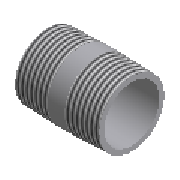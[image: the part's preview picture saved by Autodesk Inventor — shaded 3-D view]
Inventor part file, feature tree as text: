
AUTODESK INVENTOR PART (.ipt)
format: ipt  version: 2023.2 (Build 272271030, 271C)  size: 187,392 bytes
history: native  units: mm (DEFAULTED — no unit token found)
features: other x6, revolve x1, sketch x1
ambient origin geometry x8: Origin, YZ Plane, XZ Plane, XY Plane, X Axis, Y Axis, Z Axis, Center Point
bodies: Solid1 (feature_tree)
feature tree (8):
  revolve  "Revolution1"  [1 undecoded]
  other  "Work Point3"
  other  "Work Point4"
  other  "Work Axis1"
  other  "Work Point5"
  other  "Work Axis2"
  other  "Work Point6"
  sketch  "Sketch1"  dims[d12=90.0deg d1=0.312398mm d2=38.0mm d3=17.1mm d4=0.0mm d5=17.1mm d6=0.0mm d7=9.53mm d8=26.441mm d57=21.6mm d60=14.53mm d62=0.0mm]
note: 1 required parameter value undecoded (feature->parameter linkage not recoverable at this tier; creation-order binding heuristic only, values carry confidence <= 0.55)
